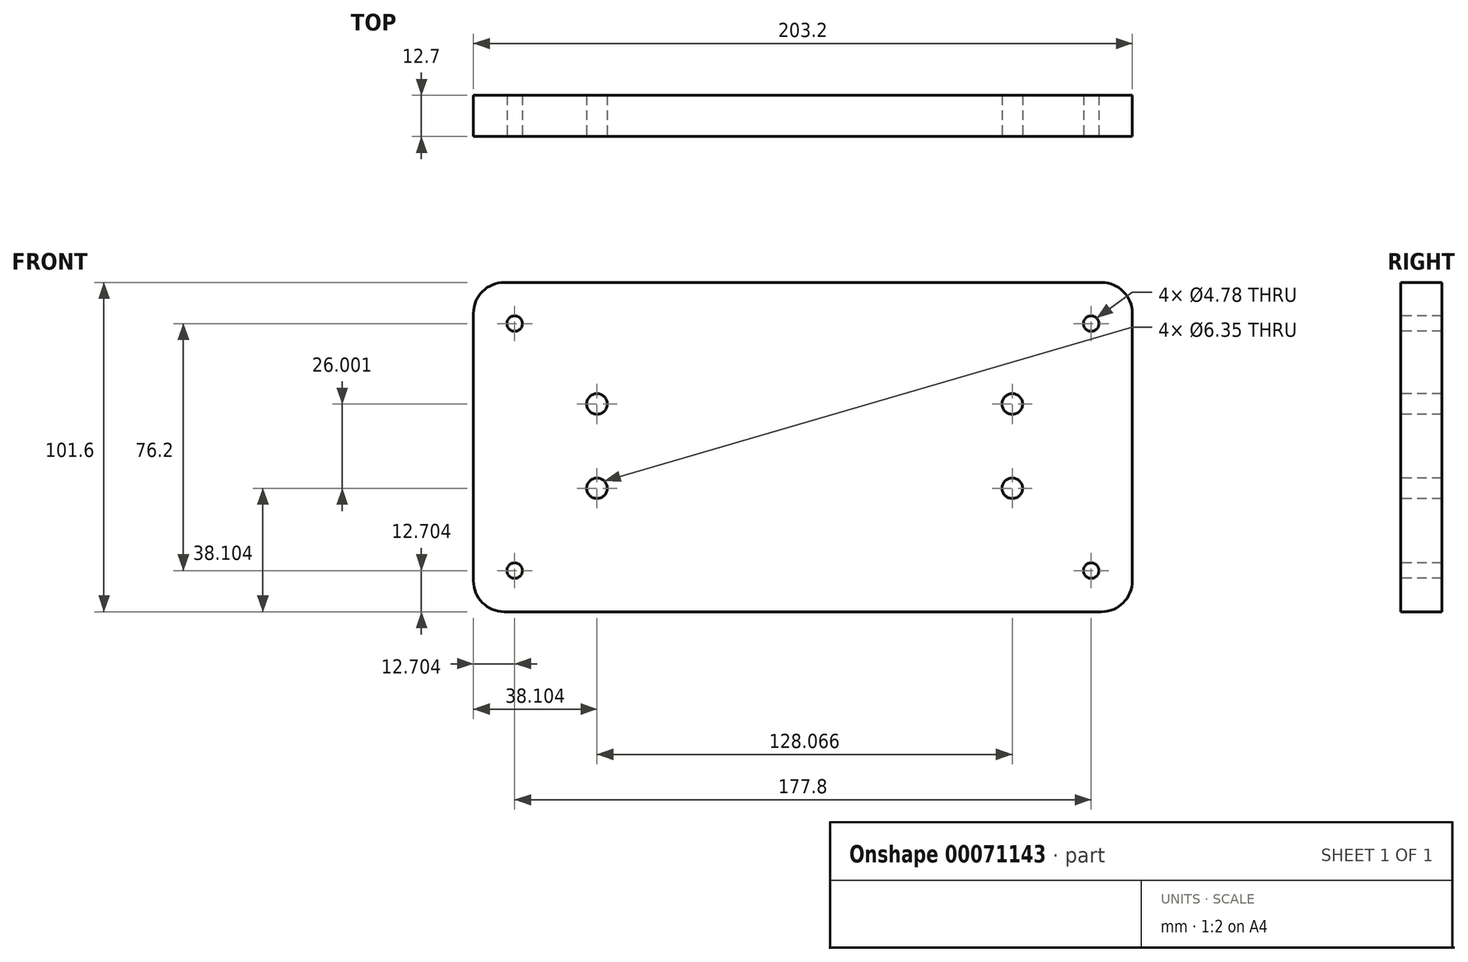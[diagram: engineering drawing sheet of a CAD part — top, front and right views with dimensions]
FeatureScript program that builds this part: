
annotation { "Feature Type Name" : "Feature", "Feature Type Description" : "" }
export const myFeature = defineFeature(function(context is Context, id is Id, definition is map)
    precondition{}
    {
        {
            var Q0;
            Q0=qCreatedBy(makeId("Front.planeOp"),FACE);
            var sketch = newSketch(context, id + "F0", { "sketchPlane" : qUnion([Q0])});
            skLineSegment(sketch, "E0.bottom", {"start": v(-99.9, 52.04) * mm, "end": v(103.3, 52.04) * mm});
            skLineSegment(sketch, "E0.top", {"start": v(-99.9, -49.56) * mm, "end": v(103.3, -49.56) * mm});
            skLineSegment(sketch, "E0.left", {"start": v(-99.9, 52.04) * mm, "end": v(-99.9, -49.56) * mm});
            skLineSegment(sketch, "E0.right", {"start": v(103.3, 52.04) * mm, "end": v(103.3, -49.56) * mm});
            skSolve(sketch);
        }
        {
            var Q0;
            Q0 = qSketchRegion(id + "F0", true);
            extrude(context, id + "F1", {"entities" : qUnion([Q0]), "depth" : 12.7 * mm});
        }
        {
            var Q0;
            Q0=makeQuery(id+"F1.opExtrude","SWEPT_EDGE",EDGE,{"disambiguationData":[OSD([sQuery(id+"F0.wireOp",EDGE,"E0.bottom"),sQuery(id+"F0.wireOp",EDGE,"E0.left")])]});
            var Q1;
            Q1=makeQuery(id+"F1.opExtrude","SWEPT_EDGE",EDGE,{"disambiguationData":[OSD([sQuery(id+"F0.wireOp",EDGE,"E0.bottom"),sQuery(id+"F0.wireOp",EDGE,"E0.right")])]});
            var Q2;
            Q2=makeQuery(id+"F1.opExtrude","SWEPT_EDGE",EDGE,{"disambiguationData":[OSD([sQuery(id+"F0.wireOp",EDGE,"E0.top"),sQuery(id+"F0.wireOp",EDGE,"E0.right")])]});
            var Q3;
            Q3=makeQuery(id+"F1.opExtrude","SWEPT_EDGE",EDGE,{"disambiguationData":[OSD([sQuery(id+"F0.wireOp",EDGE,"E0.top"),sQuery(id+"F0.wireOp",EDGE,"E0.left")])]});
            fillet(context, id + "F2", {"entities" : qUnion([Q0, Q1, Q2, Q3]), "radius" : 9.52 * mm, "tangentPropagation" : true, "allowEdgeOverflow" : false});
        }
        {
            var Q0;
            Q0=makeQuery(id+"F1.opExtrude","CAP_FACE",FACE,{"disambiguationData":[OSD([sQuery(id+"F0.wireOp",EDGE,"E0.bottom"),sQuery(id+"F0.wireOp",EDGE,"E0.top"),sQuery(id+"F0.wireOp",EDGE,"E0.left"),sQuery(id+"F0.wireOp",EDGE,"E0.right")])],"isStart":false});
            var sketch = newSketch(context, id + "F3", { "sketchPlane" : qUnion([Q0])});
            skPoint(sketch, "E1", {"position": v(-87.2, -36.86) * mm});
            skPoint(sketch, "E2", {"position": v(90.6, -36.86) * mm});
            skPoint(sketch, "E3", {"position": v(-87.2, 39.34) * mm});
            skPoint(sketch, "E4", {"position": v(90.6, 39.34) * mm});
            skSolve(sketch);
        }
        {
            var Q0;
            Q0=sQuery(id+"F3.wireOp",VERTEX,"E1");
            var Q1;
            Q1=sQuery(id+"F3.wireOp",VERTEX,"E3");
            var Q2;
            Q2=sQuery(id+"F3.wireOp",VERTEX,"E4");
            var Q3;
            Q3=sQuery(id+"F3.wireOp",VERTEX,"E2");
            var Q4;
            Q4=makeQuery(id+"F1.opExtrude","SWEPT_BODY",BODY,{"disambiguationData":[OSD([sQuery(id+"F0.wireOp",EDGE,"E0.bottom"),sQuery(id+"F0.wireOp",EDGE,"E0.top"),sQuery(id+"F0.wireOp",EDGE,"E0.left"),sQuery(id+"F0.wireOp",EDGE,"E0.right")])]});
            hole(context, id + "F4", {"style" : HoleStyle.SIMPLE, "holeDiameter" : 4.78 * mm, "endStyle" : HoleEndStyle.THROUGH, "locations" : qUnion([Q0, Q1, Q2, Q3]), "scope" : qUnion([Q4])});
        }
        {
            var Q0;
            Q0=makeQuery(id+"F1.opExtrude","CAP_FACE",FACE,{"disambiguationData":[OSD([sQuery(id+"F0.wireOp",EDGE,"E0.bottom"),sQuery(id+"F0.wireOp",EDGE,"E0.top"),sQuery(id+"F0.wireOp",EDGE,"E0.left"),sQuery(id+"F0.wireOp",EDGE,"E0.right")])],"isStart":false});
            var sketch = newSketch(context, id + "F5", { "sketchPlane" : qUnion([Q0])});
            skPoint(sketch, "E5", {"position": v(-61.8, -11.46) * mm});
            skPoint(sketch, "E6", {"position": v(-61.8, 14.54) * mm});
            skPoint(sketch, "E7", {"position": v(66.27, -11.46) * mm});
            skPoint(sketch, "E8", {"position": v(66.27, 14.54) * mm});
            skSolve(sketch);
        }
        {
            var Q0;
            Q0=sQuery(id+"F5.wireOp",VERTEX,"E6");
            var Q1;
            Q1=sQuery(id+"F5.wireOp",VERTEX,"E5");
            var Q2;
            Q2=sQuery(id+"F5.wireOp",VERTEX,"E7");
            var Q3;
            Q3=sQuery(id+"F5.wireOp",VERTEX,"E8");
            var Q4;
            Q4=makeQuery(id+"F1.opExtrude","SWEPT_BODY",BODY,{"disambiguationData":[OSD([sQuery(id+"F0.wireOp",EDGE,"E0.bottom"),sQuery(id+"F0.wireOp",EDGE,"E0.top"),sQuery(id+"F0.wireOp",EDGE,"E0.left"),sQuery(id+"F0.wireOp",EDGE,"E0.right")])]});
            hole(context, id + "F6", {"style" : HoleStyle.SIMPLE, "holeDiameter" : 6.35 * mm, "endStyle" : HoleEndStyle.THROUGH, "locations" : qUnion([Q0, Q1, Q2, Q3]), "scope" : qUnion([Q4])});
        }
    });
